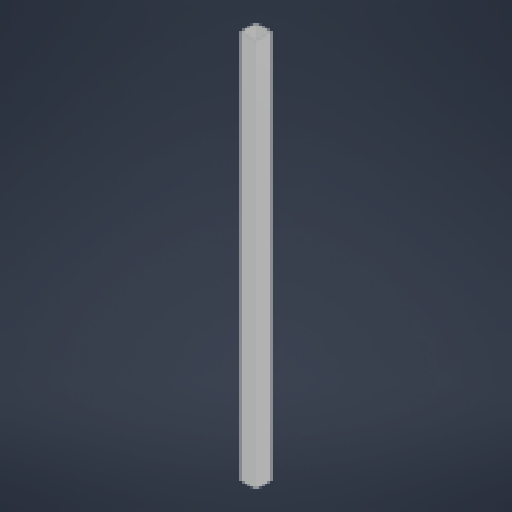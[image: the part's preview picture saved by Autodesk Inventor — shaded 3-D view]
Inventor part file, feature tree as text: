
AUTODESK INVENTOR PART (.ipt)
format: ipt  version: 2024 (Build 280153000, 153)  size: 125,952 bytes
history: native  units: mm
features: extrude x1
ambient origin geometry x8: Origin, YZ Plane, XZ Plane, XY Plane, X Axis, Y Axis, Z Axis, Center Point
bodies: Solid1 (feature_tree)
feature tree (1):
  extrude  "Extrusion1"  Depth=25.4mm
